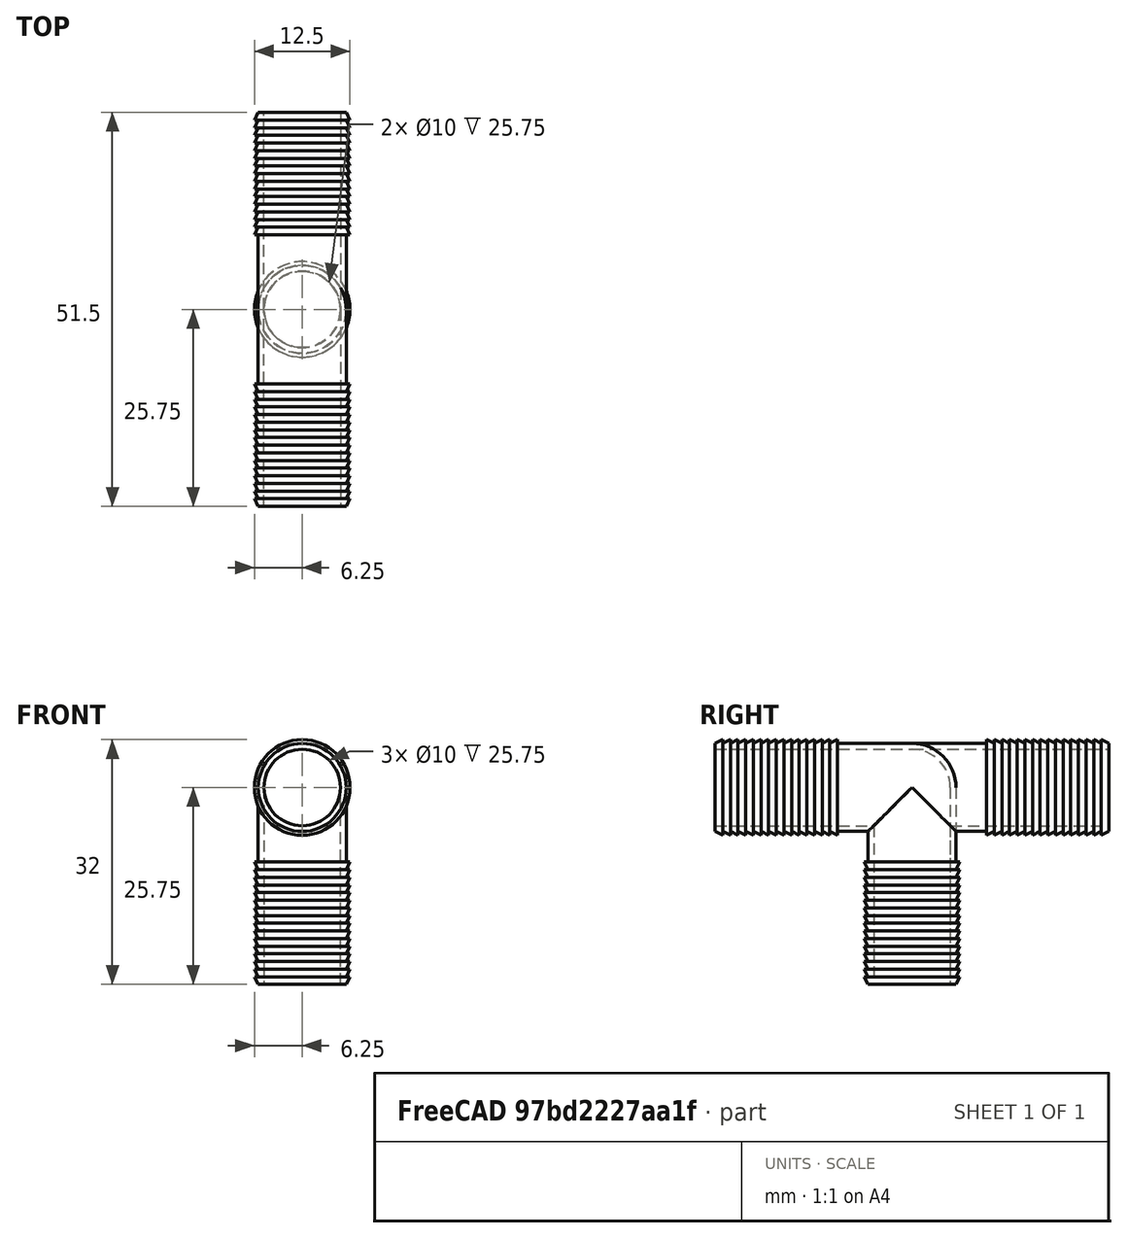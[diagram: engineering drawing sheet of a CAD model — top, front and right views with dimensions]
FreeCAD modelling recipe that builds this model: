
FCSTD DOCUMENT  (FreeCAD 1.1R1.1.0)
Label: SimpleParameterizedHoseAdapters
License: All rights reserved
LicenseURL: http://en.wikipedia.org/wiki/All_rights_reserved
objects: Part::Cylinder×8, Part::MultiFuse×6, Part::Cone×5, Part::FeaturePython×5, Part::Sphere×4, Part::Cut×2, Spreadsheet::Sheet×1
note: 25 computed .brp shape members not serialized (recipe doc carries the construction recipe); baked Part::Feature solids carry a one-line shape summary decoded from their .brp

FEATURE [Spreadsheet::Sheet] Spreadsheet  label="HoseAdapters"
  cells = A2='Inner diameter; B2(id)=10; A3='OD1; B3(od1)=11.5; A4='OD2; B4(od2)=12.5; A5='Attachment Length; B5(attachlen)=20; A6='Rips; B6(nrips)=16
FEATURE [Part::Cylinder] Cylinder
  Angle = 360
  AttacherType = Attacher::AttachEngine3D
  FirstAngle = 0
  Height = 25.75
  Radius = 5
  SecondAngle = 0
  expr: Height = <<HoseAdapters>>.attachlen + <<HoseAdapters>>.od1 / 2
  expr: Radius = <<HoseAdapters>>.id / 2
FEATURE [Part::Cylinder] Cylinder001
  Angle = 360
  AttacherType = Attacher::AttachEngine3D
  FirstAngle = 0
  Height = 25.75
  Placement = pos=(0,0,25.75) rot=(1,0,0;1.5708rad)
  Radius = 5
  SecondAngle = 0
  expr: .Placement.Base.z = <<HoseAdapters>>.attachlen + <<HoseAdapters>>.od1 / 2
  expr: Height = <<HoseAdapters>>.attachlen + <<HoseAdapters>>.od1 / 2
  expr: Radius = <<HoseAdapters>>.id / 2
FEATURE [Part::Sphere] Sphere
  Angle1 = -90
  Angle2 = 90
  Angle3 = 360
  AttacherType = Attacher::AttachEngine3D
  Placement = pos=(0,0,25.75) rot=(0,0,1;0rad)
  Radius = 5
  expr: .Placement.Base.z = <<HoseAdapters>>.attachlen + <<HoseAdapters>>.od1 / 2
  expr: Radius = <<HoseAdapters>>.id / 2
FEATURE [Part::MultiFuse] Fusion  label="InnerChannel"
  Shapes = -> [Cylinder,Cylinder001,Sphere]
FEATURE [Part::Cylinder] Cylinder002
  Angle = 360
  AttacherType = Attacher::AttachEngine3D
  FirstAngle = 0
  Height = 25.75
  Radius = 5.75
  SecondAngle = 0
  expr: Height = <<HoseAdapters>>.attachlen + <<HoseAdapters>>.od1 / 2
  expr: Radius = <<HoseAdapters>>.od1 / 2
FEATURE [Part::Cylinder] Cylinder003
  Angle = 360
  AttacherType = Attacher::AttachEngine3D
  FirstAngle = 0
  Height = 25.75
  Placement = pos=(0,0,25.75) rot=(1,0,0;1.5708rad)
  Radius = 5.75
  SecondAngle = 0
  expr: .Placement.Base.z = <<HoseAdapters>>.attachlen + <<HoseAdapters>>.od1 / 2
  expr: Height = <<HoseAdapters>>.attachlen + <<HoseAdapters>>.od1 / 2
  expr: Radius = <<HoseAdapters>>.od1 / 2
FEATURE [Part::Sphere] Sphere001
  Angle1 = -90
  Angle2 = 90
  Angle3 = 360
  AttacherType = Attacher::AttachEngine3D
  Placement = pos=(0,0,25.75) rot=(0,0,1;0rad)
  Radius = 5.75
  expr: .Placement.Base.z = <<HoseAdapters>>.attachlen + <<HoseAdapters>>.od1 / 2
  expr: Radius = <<HoseAdapters>>.od1 / 2
FEATURE [Part::MultiFuse] Fusion001  label="OuterMain"
  Shapes = -> [Cylinder002,Cylinder003,Sphere001]
FEATURE [Part::Cone] Cone
  Angle = 360
  AttacherType = Attacher::AttachEngine3D
  Height = 1
  Radius1 = 5.75
  Radius2 = 6.25
  expr: Height = <<HoseAdapters>>.od2 - <<HoseAdapters>>.od1
  expr: Radius1 = <<HoseAdapters>>.od1 / 2
  expr: Radius2 = <<HoseAdapters>>.od2 / 2
FEATURE [Part::FeaturePython] Array  # Draft array (typed FeaturePython)
  AlwaysSyncPlacement = false
  Angle = 360
  ArrayType = 0
  Axis = (0,0,1)
  Base = -> Cone
  Center = (0,0,0)
  Count = 16
  ExpandArray = false
  Fuse = false
  IntervalAxis = (0,0,0)
  IntervalX = (100,0,0)
  IntervalY = (0,100,0)
  IntervalZ = (0,0,1)
  NumberCircles = 3
  NumberPolar = 5
  NumberX = 1
  NumberY = 1
  NumberZ = 16
  PlacementList = 16 placements: arithmetic series from (0,0,0) step (0,0,1) to (0,0,15)
  RadialDistance = 50
  ScaleList = (16) [(1,1,1),(1,1,1),(1,1,1),(1,1,1),(1,1,1),(1,1,1),(1,1,1),(1,1,1),(1,1,1),(1,1,1),(1,1,1),(1,1,1),(1,1,1),(1,1,1),(1,1,1),(1,1,1)]
  Symmetry = 1
  TangentialDistance = 25
  expr: .IntervalZ.z = <<HoseAdapters>>.od2 - <<HoseAdapters>>.od1
  expr: NumberZ = <<HoseAdapters>>.nrips
FEATURE [Part::Cone] Cone002
  Angle = 360
  AttacherType = Attacher::AttachEngine3D
  Height = 1
  Radius1 = 5.75
  Radius2 = 6.25
  expr: Height = <<HoseAdapters>>.od2 - <<HoseAdapters>>.od1
  expr: Radius1 = <<HoseAdapters>>.od1 / 2
  expr: Radius2 = <<HoseAdapters>>.od2 / 2
FEATURE [Part::FeaturePython] Array001  # Draft array (typed FeaturePython)
  AlwaysSyncPlacement = false
  Angle = 360
  ArrayType = 0
  Axis = (0,0,1)
  Base = -> Cone002
  Center = (0,0,0)
  Count = 16
  ExpandArray = false
  Fuse = false
  IntervalAxis = (0,0,0)
  IntervalX = (100,0,0)
  IntervalY = (0,100,0)
  IntervalZ = (0,0,1)
  NumberCircles = 3
  NumberPolar = 5
  NumberX = 1
  NumberY = 1
  NumberZ = 16
  Placement = pos=(0,-25.75,25.75) rot=(1,0,0;-1.5708rad)
  PlacementList = 16 placements: arithmetic series from (0,0,0) step (0,0,1) to (0,0,15)
  RadialDistance = 50
  ScaleList = (16) [(1,1,1),(1,1,1),(1,1,1),(1,1,1),(1,1,1),(1,1,1),(1,1,1),(1,1,1),(1,1,1),(1,1,1),(1,1,1),(1,1,1),(1,1,1),(1,1,1),(1,1,1),(1,1,1)]
  Symmetry = 1
  TangentialDistance = 25
  expr: .IntervalZ.z = <<HoseAdapters>>.od2 - <<HoseAdapters>>.od1
  expr: .Placement.Base.y = -<<HoseAdapters>>.attachlen - <<HoseAdapters>>.od1 / 2
  expr: .Placement.Base.z = <<HoseAdapters>>.attachlen + <<HoseAdapters>>.od1 / 2
  expr: NumberZ = <<HoseAdapters>>.nrips
FEATURE [Part::MultiFuse] Fusion002  label="OuterBody"
  Shapes = -> [Array,Array001,Fusion001]
FEATURE [Part::Cut] Cut  label="HoseL"
  Base = -> Fusion002
  Tool = -> Fusion
FEATURE [Part::Cone] Cone003
  Angle = 360
  AttacherType = Attacher::AttachEngine3D
  Height = 1
  Radius1 = 5.75
  Radius2 = 6.25
  expr: Height = <<HoseAdapters>>.od2 - <<HoseAdapters>>.od1
  expr: Radius1 = <<HoseAdapters>>.od1 / 2
  expr: Radius2 = <<HoseAdapters>>.od2 / 2
FEATURE [Part::FeaturePython] Array002  # Draft array (typed FeaturePython)
  AlwaysSyncPlacement = false
  Angle = 360
  ArrayType = 0
  Axis = (0,0,1)
  Base = -> Cone003
  Center = (0,0,0)
  Count = 16
  ExpandArray = false
  Fuse = false
  IntervalAxis = (0,0,0)
  IntervalX = (100,0,0)
  IntervalY = (0,100,0)
  IntervalZ = (0,0,1)
  NumberCircles = 3
  NumberPolar = 5
  NumberX = 1
  NumberY = 1
  NumberZ = 16
  PlacementList = 16 placements: arithmetic series from (0,0,0) step (0,0,1) to (0,0,15)
  RadialDistance = 50
  ScaleList = (16) [(1,1,1),(1,1,1),(1,1,1),(1,1,1),(1,1,1),(1,1,1),(1,1,1),(1,1,1),(1,1,1),(1,1,1),(1,1,1),(1,1,1),(1,1,1),(1,1,1),(1,1,1),(1,1,1)]
  Symmetry = 1
  TangentialDistance = 25
  expr: .IntervalZ.z = <<HoseAdapters>>.od2 - <<HoseAdapters>>.od1
  expr: NumberZ = <<HoseAdapters>>.nrips
FEATURE [Part::Cone] Cone004
  Angle = 360
  AttacherType = Attacher::AttachEngine3D
  Height = 1
  Radius1 = 5.75
  Radius2 = 6.25
  expr: Height = <<HoseAdapters>>.od2 - <<HoseAdapters>>.od1
  expr: Radius1 = <<HoseAdapters>>.od1 / 2
  expr: Radius2 = <<HoseAdapters>>.od2 / 2
FEATURE [Part::FeaturePython] Array003  # Draft array (typed FeaturePython)
  AlwaysSyncPlacement = false
  Angle = 360
  ArrayType = 0
  Axis = (0,0,1)
  Base = -> Cone004
  Center = (0,0,0)
  Count = 16
  ExpandArray = false
  Fuse = false
  IntervalAxis = (0,0,0)
  IntervalX = (100,0,0)
  IntervalY = (0,100,0)
  IntervalZ = (0,0,1)
  NumberCircles = 3
  NumberPolar = 5
  NumberX = 1
  NumberY = 1
  NumberZ = 16
  Placement = pos=(0,-25.75,25.75) rot=(1,0,0;-1.5708rad)
  PlacementList = 16 placements: arithmetic series from (0,0,0) step (0,0,1) to (0,0,15)
  RadialDistance = 50
  ScaleList = (16) [(1,1,1),(1,1,1),(1,1,1),(1,1,1),(1,1,1),(1,1,1),(1,1,1),(1,1,1),(1,1,1),(1,1,1),(1,1,1),(1,1,1),(1,1,1),(1,1,1),(1,1,1),(1,1,1)]
  Symmetry = 1
  TangentialDistance = 25
  expr: .IntervalZ.z = <<HoseAdapters>>.od2 - <<HoseAdapters>>.od1
  expr: .Placement.Base.y = -<<HoseAdapters>>.attachlen - <<HoseAdapters>>.od1 / 2
  expr: .Placement.Base.z = <<HoseAdapters>>.attachlen + <<HoseAdapters>>.od1 / 2
  expr: NumberZ = <<HoseAdapters>>.nrips
FEATURE [Part::Cylinder] Cylinder004
  Angle = 360
  AttacherType = Attacher::AttachEngine3D
  FirstAngle = 0
  Height = 25.75
  Radius = 5
  SecondAngle = 0
  expr: Height = <<HoseAdapters>>.attachlen + <<HoseAdapters>>.od1 / 2
  expr: Radius = <<HoseAdapters>>.id / 2
FEATURE [Part::Cylinder] Cylinder005
  Angle = 360
  AttacherType = Attacher::AttachEngine3D
  FirstAngle = 0
  Height = 51.5
  Placement = pos=(0,25.75,25.75) rot=(1,0,0;1.5708rad)
  Radius = 5
  SecondAngle = 0
  expr: .Placement.Base.y = <<HoseAdapters>>.attachlen + <<HoseAdapters>>.od1 / 2
  expr: .Placement.Base.z = <<HoseAdapters>>.attachlen + <<HoseAdapters>>.od1 / 2
  expr: Height = 2 * (<<HoseAdapters>>.attachlen + <<HoseAdapters>>.od1 / 2)
  expr: Radius = <<HoseAdapters>>.id / 2
FEATURE [Part::Cylinder] Cylinder006
  Angle = 360
  AttacherType = Attacher::AttachEngine3D
  FirstAngle = 0
  Height = 25.75
  Radius = 5.75
  SecondAngle = 0
  expr: Height = <<HoseAdapters>>.attachlen + <<HoseAdapters>>.od1 / 2
  expr: Radius = <<HoseAdapters>>.od1 / 2
FEATURE [Part::Cylinder] Cylinder007
  Angle = 360
  AttacherType = Attacher::AttachEngine3D
  FirstAngle = 0
  Height = 51.5
  Placement = pos=(0,25.75,25.75) rot=(1,0,0;1.5708rad)
  Radius = 5.75
  SecondAngle = 0
  expr: .Placement.Base.y = <<HoseAdapters>>.attachlen + <<HoseAdapters>>.od1 / 2
  expr: .Placement.Base.z = <<HoseAdapters>>.attachlen + <<HoseAdapters>>.od1 / 2
  expr: Height = (<<HoseAdapters>>.attachlen + <<HoseAdapters>>.od1 / 2) * 2
  expr: Radius = <<HoseAdapters>>.od1 / 2
FEATURE [Part::Sphere] Sphere002
  Angle1 = -90
  Angle2 = 90
  Angle3 = 360
  AttacherType = Attacher::AttachEngine3D
  Placement = pos=(0,0,25.75) rot=(0,0,1;0rad)
  Radius = 5
  expr: .Placement.Base.z = <<HoseAdapters>>.attachlen + <<HoseAdapters>>.od1 / 2
  expr: Radius = <<HoseAdapters>>.id / 2
FEATURE [Part::MultiFuse] Fusion003  label="InnerChannel001"
  Shapes = -> [Cylinder004,Cylinder005,Sphere002]
FEATURE [Part::Sphere] Sphere003
  Angle1 = -90
  Angle2 = 90
  Angle3 = 360
  AttacherType = Attacher::AttachEngine3D
  Placement = pos=(0,0,25.75) rot=(0,0,1;0rad)
  Radius = 5.75
  expr: .Placement.Base.z = <<HoseAdapters>>.attachlen + <<HoseAdapters>>.od1 / 2
  expr: Radius = <<HoseAdapters>>.od1 / 2
FEATURE [Part::MultiFuse] Fusion004  label="OuterMain001"
  Shapes = -> [Cylinder006,Cylinder007,Sphere003]
FEATURE [Part::Cone] Cone005
  Angle = 360
  AttacherType = Attacher::AttachEngine3D
  Height = 1
  Radius1 = 5.75
  Radius2 = 6.25
  expr: Height = <<HoseAdapters>>.od2 - <<HoseAdapters>>.od1
  expr: Radius1 = <<HoseAdapters>>.od1 / 2
  expr: Radius2 = <<HoseAdapters>>.od2 / 2
FEATURE [Part::FeaturePython] Array004  # Draft array (typed FeaturePython)
  AlwaysSyncPlacement = false
  Angle = 360
  ArrayType = 0
  Axis = (0,0,1)
  Base = -> Cone005
  Center = (0,0,0)
  Count = 16
  ExpandArray = false
  Fuse = false
  IntervalAxis = (0,0,0)
  IntervalX = (100,0,0)
  IntervalY = (0,100,0)
  IntervalZ = (0,0,1)
  NumberCircles = 3
  NumberPolar = 5
  NumberX = 1
  NumberY = 1
  NumberZ = 16
  Placement = pos=(0,25.75,25.75) rot=(1,0,0;1.5708rad)
  PlacementList = 16 placements: arithmetic series from (0,0,0) step (0,0,1) to (0,0,15)
  RadialDistance = 50
  ScaleList = (16) [(1,1,1),(1,1,1),(1,1,1),(1,1,1),(1,1,1),(1,1,1),(1,1,1),(1,1,1),(1,1,1),(1,1,1),(1,1,1),(1,1,1),(1,1,1),(1,1,1),(1,1,1),(1,1,1)]
  Symmetry = 1
  TangentialDistance = 25
  expr: .IntervalZ.z = <<HoseAdapters>>.od2 - <<HoseAdapters>>.od1
  expr: .Placement.Base.y = <<HoseAdapters>>.attachlen + <<HoseAdapters>>.od1 / 2
  expr: .Placement.Base.z = <<HoseAdapters>>.attachlen + <<HoseAdapters>>.od1 / 2
  expr: NumberZ = <<HoseAdapters>>.nrips
FEATURE [Part::MultiFuse] Fusion005  label="OuterBody001"
  Shapes = -> [Array002,Array003,Fusion004,Array004]
FEATURE [Part::Cut] Cut001  label="HoseT"
  Base = -> Fusion005
  Tool = -> Fusion003
